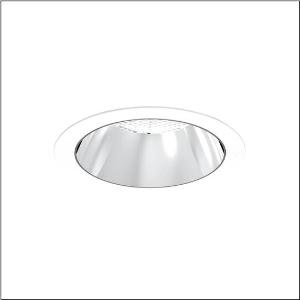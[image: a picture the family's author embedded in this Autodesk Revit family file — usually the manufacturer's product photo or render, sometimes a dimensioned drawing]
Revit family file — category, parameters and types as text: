
# Revit family: lunis_21_xl_51db15tf91c
name_source: partatom
category: Lighting Fixtures
units: mm (PartAtom-declared; Revit-internal decimal feet)

## family parameters
Cut with Voids When Loaded = No
Host = Face
Light Source = No
Part Type = Normal
Room Calculation Point = No
Round Connector Dimension = Use Diameter
Shared = No

## types (1)
- --- (1 x LED, 4150 lm, 25.4 W, 4000K)
    Apparent Load = 25 VA
    CIE Flux Codes = 95 98 100 100 100
    Color Rendering = 80
    Color Temperature = 4000K
    Default Elevation = 1800 mm
    Description = Lunis 21,  XL, downlight, light control with lens, of PMMA, anti glare with reflector, of aluminium, highly specular, light emission: direct distribution, LED rated luminous flux: 2.430lm, light colour: 8tw, with terminal, 5-pole, mains connection: 220..240V, AC/DC, 0/50..60Hz, housing, round, of diecast aluminium, traffic white (RAL 9016), diameter: 230mm, clamping range: 1..40mm, protection rating (complete): IP20, protection rating (on room side): IP54, insulation class (complete): insulation class II (safety insulation), certification: CE, impact resistance: IK03, packaging unit: 1 piece
    Height = 0 mm  [stored 0 ft]
    Lamp = 1 x LED
    Lamp Light Flux = 4150 lm
    Lamp Power = 25.4 W
    Lamp count = 1
    Length = 230 mm
    Luminous efficacy = 163 lm/W
    Manufacturer = Siteco
    ModVariant = No
    Model = 51DB15TF91C
    Mounting Place = Ceiling
    Mounting Type = Recessed
    Number of Poles = 1
    OnlyDefault = Yes
    Power Factor = 1
    Product Name = Lunis 21 XL
    Product group = downlight
    ProductGroupID = 400
    Protection Class = Protection class II
    Protection Degree = IP 20
    RLX_Detail_Level = 1
    RLX_Emergency_Light_Flux = 0 lm
    RLX_Emergency_Type = 0
    RLX_Emergency_Type_DB = No
    RlxData = <blob elided: 18825 chars, md5=e88ea746>
    Socket = socket
    Standby Power = 0 W
    System Light Flux = 4150 lm
    System Power = 25 W
    Type Comments = individual setting: colour temperature 4000K, luminous flux: 100 % | (ON | ON | OFF | OFF) | 700 mA
    Type Image = l_1291156.jpg
    URL = http://relux.com
    VarID = @adj_018973
    Voltage = 0 V
    Weight = 0.00 kg
    Width = 0 mm  [stored 0 ft]

note: [stored X ft] marks values corroborated as IEEE doubles in the binary element streams (Revit-internal decimal feet)

## geometry (parser evidence)
native form markers: Blend x4, Sweep x11
no freeform markers — native parametric forms only
